# Revit family: IS_CeraplanIII_BC569_BIM_GB
name_source: partatom
category: Plumbing Fixtures
revit_build: Autodesk Revit 2017 (Build: 20160225_1515(x64)
units: mm (PartAtom-declared; Revit-internal decimal feet)

## family parameters
Always vertical = No
Cut with Voids When Loaded = No
OmniClass Number = 23.45.55.17
OmniClass Title = Mixing Faucets
Part Type = Normal
Room Calculation Point = No
Round Connector Dimension = Use Diameter
Shared = No
Work Plane-Based = No

## types (1)
- BC569AA - CERAPLAN III BSN MXR H90 RM 5LPM CH3
    Accessories = https://www.idealspec.co.uk
    AreaUnits = millimeters
    AssetType = Fixed
    BIMObjectName = ISI_IdealStandard_Washbasintaps_CeraplanIII_BC569
    BIMobject category = Taps & Mixers
    BIMobject category code = sanitary-taps-mixers
    BIMobject main category = Sanitary
    BIMobject main category code = sanitary
    BarCode = 3800861080633
    Brand url = http://www.idealstandard.co.uk
    Color = Chrome
    ConnectionType = Plumbing
    CurrencyUnit = £
    CurrentRevision = 1
    Date of publishing = 15/09/2020
    Description = CERAPLAN III Single lever basin mixer 156 (H95) DN 15 BlueStart with 109 mm spout projection. Rigid cast spout and aerator with metal ring. Base diameter 47mm. Flexible connecting hose and metal lever. Chrome Finish
    DrainSize = 0 mm  [stored 0 ft]
    DurationUnit = Year
    Edition number = 1
    ExpectedLife = 30
    FaucetFunction = MIXED
    FaucetOperation = OTHER
    FaucetType = OTHER
    Features = Single lever basin mixer 156 (H95) DN 15 BlueStart with 109 mm spout projection. Rigid cast spout and aerator with metal ring. Base diameter 47mm. Flexible connecting hose and metal lever. Chrome Finish
    Finish = Chrome
    GTIN code = https://3800861080633
    IFC Classification = Sanitary Terminal
    IfcExportAs = IfcValveType
    IfcExportType = FAUCET
    InletConnectionSize = 0 mm  [stored 0 ft]
    Installation instructions = https://www.idealspec.co.uk
    InstallationInstructions = https://www.idealspec.co.uk
    IsHighPressure = No
    LinearUnits = millimeters
    MainColor = Chrome
    MaintenanceInformation = https://www.idealspec.co.uk
    Manufacturer = Ideal Standard (UK) Ltd
    Manufacturer name = Ideal Standard
    ManufacturerURL = https://www.idealspec.co.uk
    Material = Brass
    Material main = Brass
    MaterialThickness = 0 mm  [stored 0 ft]
    Model = BC569AA
    ModelNumber = BC569AA
    ModelReference = CERAPLAN III BSN MXR H90 RM 5LPM CH3
    NBS Reference Code = 45-35-70/371
    NBS Reference Description = Water supply fittings for wash basins and troughs;
    Name = Washbasintaps_CeraplanIII_BC569_IdealStandard
    NettWeight = 1,36 KG
    NominalDepth = 147 mm
    NominalHeight = 156 mm
    NominalLength = 147 mm
    NominalWidth = 48 mm
    OmniClass Code = 23-31 11 00
    OmniClass Description = Faucets
    Product Guid = 1f33a07b-b55e-4cf0-bd63-5bb60ffaa9d6
    Product SKU = BC569
    Product certification = https://www.idealspec.co.uk
    Product data url = https://bimobject.com
    Product family = CERAPLAN III
    Product group = Basin Mixer
    Product name = A_CERAPLAN III BSN MXR H90 RM 5LPM CH3
    Product url = https://www.idealspec.co.uk
    ProductInformation = https://www.idealspec.co.uk
    QR code = http://bimobject.com
    Shape = Sculptured
    Size = 48 x 147 x 156 mm
    Space = Internal
    SpareParts = https://fastpart-spares.co.uk
    Technical description = https://www.idealspec.co.uk
    TestPressure = 10 Bar
    UNSPSC Code = 301815
    URL = https://www.idealspec.co.uk
    Uniclass 1.4 Code = L725111
    Uniclass 1.4 Description = Mixer taps
    Uniclass 2.0 Code = Pr_40_30_96_96
    Uniclass 2.0 Description = Washbasin Manual Water Supply Sets
    Uniclass 2015 Code = Pr_40_20_87_98
    Uniclass 2015 Name = Washbasin taps
    Uniclass2015Code = Pr_40_20_87_98
    Uniclass2015Title = Washbasin taps
    Uniclass2015Version = v1.1
    ValveOperation = Lever
    Version = 1
    VolumeUnits = Litres
    WRASURL = https://www.wras.co.uk
    WarrantyDescription = Manufacturers Warranty
    WarrantyDurationParts = https://www.idealspec.co.uk
    WarrantyDurationUnit = Year
    WarrantyGuarantorParts = https://www.idealspec.co.uk

note: [stored X ft] marks values corroborated as IEEE doubles in the binary element streams (Revit-internal decimal feet)

## geometry (parser evidence)
native form markers: Sweep x2
no freeform markers — native parametric forms only
